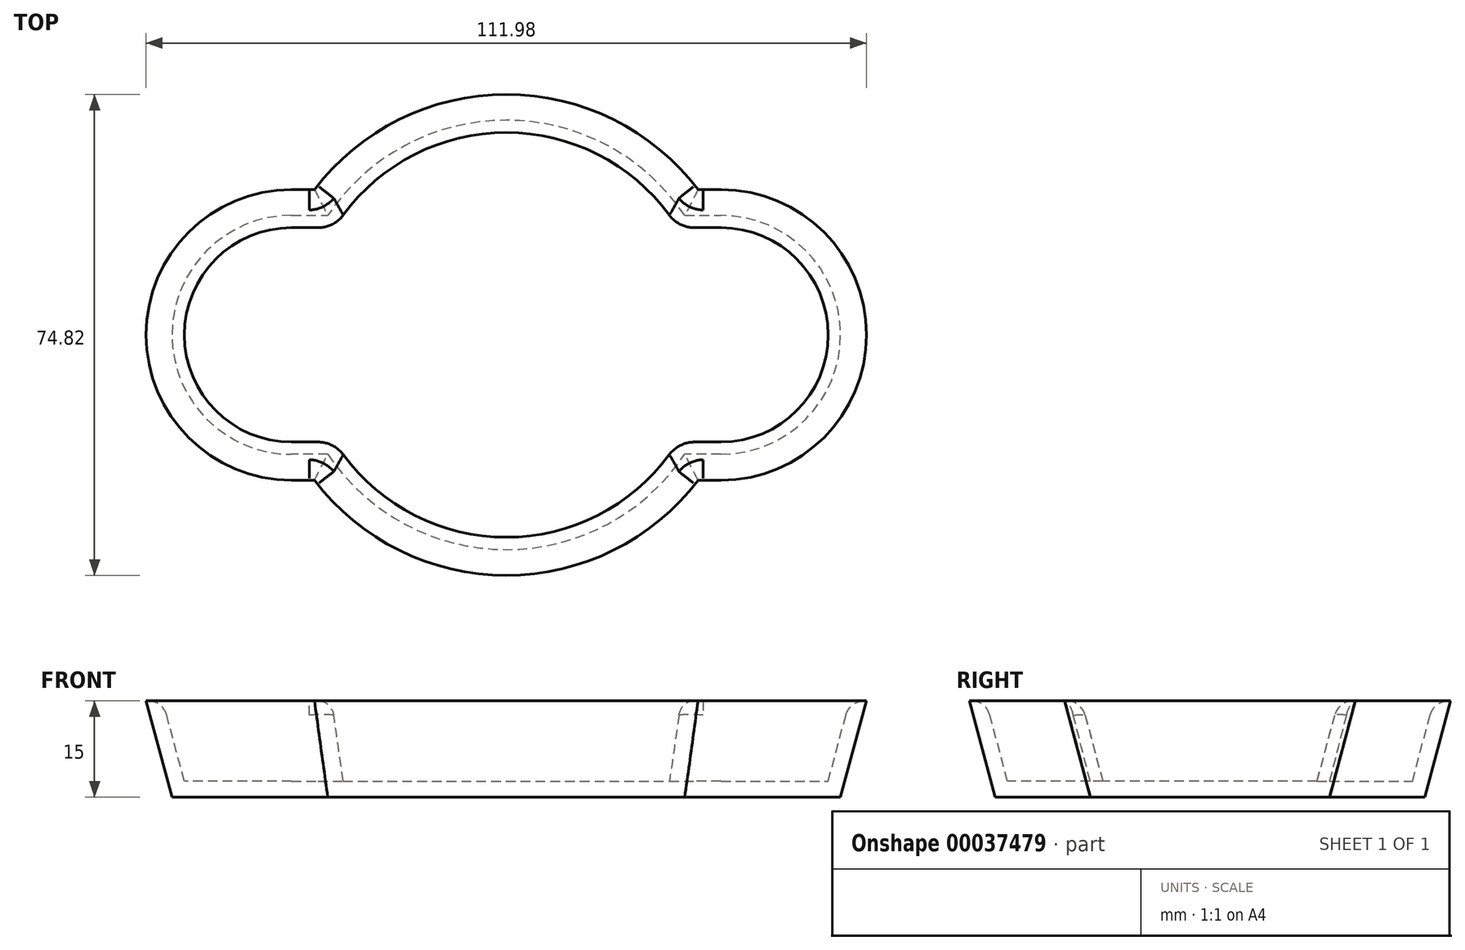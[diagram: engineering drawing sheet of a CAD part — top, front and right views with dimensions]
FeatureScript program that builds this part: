
annotation { "Feature Type Name" : "Feature", "Feature Type Description" : "" }
export const myFeature = defineFeature(function(context is Context, id is Id, definition is map)
    precondition{}
    {
        {
            var Q0;
            Q0=qCreatedBy(makeId("Top.planeOp"),FACE);
            var sketch = newSketch(context, id + "F0", { "sketchPlane" : qUnion([Q0])});
            skArc(sketch, "E0", {"start": v(-27.74, -18.58) * mm, "mid": v(0, -33.39) * mm, "end": v(27.74, -18.58) * mm});
            skArc(sketch, "E1", {"start": v(33.39, -18.58) * mm, "mid": v(51.97, 0) * mm, "end": v(33.39, 18.58) * mm});
            skLineSegment(sketch, "E2", {"start": v(0, 58.58) * mm, "end": v(0, -59.96) * mm, "construction": true});
            skArc(sketch, "E3.MirrorC", {"start": v(-33.39, -18.58) * mm, "mid": v(-51.97, 0) * mm, "end": v(-33.39, 18.58) * mm});
            skArc(sketch, "E4.trimOffspring", {"start": v(27.74, 18.58) * mm, "mid": v(0, 33.39) * mm, "end": v(-27.74, 18.58) * mm});
            skLineSegment(sketch, "E5", {"start": v(-33.39, 18.58) * mm, "end": v(-27.74, 18.58) * mm});
            skLineSegment(sketch, "E6", {"start": v(-33.39, -18.58) * mm, "end": v(-27.74, -18.58) * mm});
            skLineSegment(sketch, "E7.trimOffspring", {"start": v(27.74, 18.58) * mm, "end": v(33.39, 18.58) * mm});
            skLineSegment(sketch, "E8.trimOffspring", {"start": v(27.74, -18.58) * mm, "end": v(33.39, -18.58) * mm});
            skSolve(sketch);
        }
        {
            var Q0;
            Q0=qCreatedBy(makeId("Top.planeOp"),FACE);
            cPlane(context, id + "F1", {"entities" : qUnion([Q0]), "cplaneType" : CPlaneType.OFFSET, "offset" : 15 * mm, "width" : 152.4 * mm, "height" : 152.4 * mm});
        }
        {
            var Q0;
            Q0 = qSketchRegion(id + "F0", true);
            extrude(context, id + "F2", {"entities" : qUnion([Q0]), "depth" : 15 * mm, "hasDraft" : true, "draftAngle" : 15 * degree});
        }
        {
            var Q0;
            Q0=makeQuery(id+"F2.opExtrude","CAP_FACE",FACE,{"disambiguationData":[OSD([sQuery(id+"F0.wireOp",EDGE,"E0"),sQuery(id+"F0.wireOp",EDGE,"E1"),sQuery(id+"F0.wireOp",EDGE,"E3.MirrorC"),sQuery(id+"F0.wireOp",EDGE,"E4.trimOffspring"),sQuery(id+"F0.wireOp",EDGE,"E5"),sQuery(id+"F0.wireOp",EDGE,"E6"),sQuery(id+"F0.wireOp",EDGE,"E7.trimOffspring"),sQuery(id+"F0.wireOp",EDGE,"E8.trimOffspring")])],"isStart":false});
            shell(context, id + "F3", {"entities" : qUnion([Q0]), "thickness" : 2.5 * mm});
        }
        {
            var Q0;
            {var subQ0=sQuery(id+"F0.wireOp",EDGE,"E3.MirrorC");Q0=makeQuery(id+"F3.opShell","OFFSET_EDGE",EDGE,{"disambiguationData":[OSD([subQ0]),TDD([makeQuery(id+"F2.opExtrude","CAP_EDGE",EDGE,{"disambiguationData":[OSD([subQ0])],"isStart":false})])]});}
            var Q1;
            {var subQ0=sQuery(id+"F0.wireOp",EDGE,"E4.trimOffspring");Q1=makeQuery(id+"F3.opShell","OFFSET_EDGE",EDGE,{"disambiguationData":[OSD([subQ0]),TDD([makeQuery(id+"F2.opExtrude","CAP_EDGE",EDGE,{"disambiguationData":[OSD([subQ0])],"isStart":false})])]});}
            var Q2;
            {var subQ0=sQuery(id+"F0.wireOp",EDGE,"E5");Q2=makeQuery(id+"F3.opShell","OFFSET_EDGE",EDGE,{"disambiguationData":[OSD([subQ0]),TDD([makeQuery(id+"F2.opExtrude","CAP_EDGE",EDGE,{"disambiguationData":[OSD([subQ0])],"isStart":false})])]});}
            var Q3;
            {var subQ0=sQuery(id+"F0.wireOp",EDGE,"E7.trimOffspring");Q3=makeQuery(id+"F3.opShell","OFFSET_EDGE",EDGE,{"disambiguationData":[OSD([subQ0]),TDD([makeQuery(id+"F2.opExtrude","CAP_EDGE",EDGE,{"disambiguationData":[OSD([subQ0])],"isStart":false})])]});}
            var Q4;
            {var subQ0=sQuery(id+"F0.wireOp",EDGE,"E1");Q4=makeQuery(id+"F3.opShell","OFFSET_EDGE",EDGE,{"disambiguationData":[OSD([subQ0]),TDD([makeQuery(id+"F2.opExtrude","CAP_EDGE",EDGE,{"disambiguationData":[OSD([subQ0])],"isStart":false})])]});}
            var Q5;
            {var subQ0=sQuery(id+"F0.wireOp",EDGE,"E0");Q5=makeQuery(id+"F3.opShell","OFFSET_EDGE",EDGE,{"disambiguationData":[OSD([subQ0]),TDD([makeQuery(id+"F2.opExtrude","CAP_EDGE",EDGE,{"disambiguationData":[OSD([subQ0])],"isStart":false})])]});}
            var Q6;
            {var subQ0=sQuery(id+"F0.wireOp",EDGE,"E8.trimOffspring");Q6=makeQuery(id+"F3.opShell","OFFSET_EDGE",EDGE,{"disambiguationData":[OSD([subQ0]),TDD([makeQuery(id+"F2.opExtrude","CAP_EDGE",EDGE,{"disambiguationData":[OSD([subQ0])],"isStart":false})])]});}
            var Q7;
            {var subQ0=sQuery(id+"F0.wireOp",EDGE,"E6");Q7=makeQuery(id+"F3.opShell","OFFSET_EDGE",EDGE,{"disambiguationData":[OSD([subQ0]),TDD([makeQuery(id+"F2.opExtrude","CAP_EDGE",EDGE,{"disambiguationData":[OSD([subQ0])],"isStart":false})])]});}
            fillet(context, id + "F4", {"entities" : qUnion([Q0, Q1, Q2, Q3, Q4, Q5, Q6, Q7]), "radius" : 3 * mm, "tangentPropagation" : true, "allowEdgeOverflow" : false});
        }
        {
            var Q0;
            {var subQ0=sQuery(id+"F0.wireOp",EDGE,"E6");var subQ1=sQuery(id+"F0.wireOp",EDGE,"E0");Q0=makeQuery(id+"F4.opFillet","BLEND_EDGE",EDGE,{"blendedFrom":[makeQuery(id+"F3.opShell","OFFSET_EDGE",EDGE,{"disambiguationData":[OSD([subQ1]),TDD([makeQuery(id+"F2.opExtrude","CAP_EDGE",EDGE,{"disambiguationData":[OSD([subQ1])],"isStart":false})])]}),makeQuery(id+"F3.opShell","OFFSET_EDGE",EDGE,{"disambiguationData":[OSD([subQ0]),TDD([makeQuery(id+"F2.opExtrude","CAP_EDGE",EDGE,{"disambiguationData":[OSD([subQ0])],"isStart":false})])]})],"blendedInto":[]});}
            var Q1;
            Q1=makeQuery(id+"F3.opShell","OFFSET_EDGE",EDGE,{"disambiguationData":[OSD([sQuery(id+"F0.wireOp",EDGE,"E0"),sQuery(id+"F0.wireOp",EDGE,"E6")])]});
            var Q2;
            {var subQ0=sQuery(id+"F0.wireOp",EDGE,"E8.trimOffspring");var subQ1=sQuery(id+"F0.wireOp",EDGE,"E0");Q2=makeQuery(id+"F4.opFillet","BLEND_EDGE",EDGE,{"blendedFrom":[makeQuery(id+"F3.opShell","OFFSET_EDGE",EDGE,{"disambiguationData":[OSD([subQ1]),TDD([makeQuery(id+"F2.opExtrude","CAP_EDGE",EDGE,{"disambiguationData":[OSD([subQ1])],"isStart":false})])]}),makeQuery(id+"F3.opShell","OFFSET_EDGE",EDGE,{"disambiguationData":[OSD([subQ0]),TDD([makeQuery(id+"F2.opExtrude","CAP_EDGE",EDGE,{"disambiguationData":[OSD([subQ0])],"isStart":false})])]})],"blendedInto":[]});}
            var Q3;
            Q3=makeQuery(id+"F3.opShell","OFFSET_EDGE",EDGE,{"disambiguationData":[OSD([sQuery(id+"F0.wireOp",EDGE,"E0"),sQuery(id+"F0.wireOp",EDGE,"E8.trimOffspring")])]});
            var Q4;
            {var subQ0=sQuery(id+"F0.wireOp",EDGE,"E7.trimOffspring");var subQ1=sQuery(id+"F0.wireOp",EDGE,"E4.trimOffspring");Q4=makeQuery(id+"F4.opFillet","BLEND_EDGE",EDGE,{"blendedFrom":[makeQuery(id+"F3.opShell","OFFSET_EDGE",EDGE,{"disambiguationData":[OSD([subQ1]),TDD([makeQuery(id+"F2.opExtrude","CAP_EDGE",EDGE,{"disambiguationData":[OSD([subQ1])],"isStart":false})])]}),makeQuery(id+"F3.opShell","OFFSET_EDGE",EDGE,{"disambiguationData":[OSD([subQ0]),TDD([makeQuery(id+"F2.opExtrude","CAP_EDGE",EDGE,{"disambiguationData":[OSD([subQ0])],"isStart":false})])]})],"blendedInto":[]});}
            var Q5;
            Q5=makeQuery(id+"F3.opShell","OFFSET_EDGE",EDGE,{"disambiguationData":[OSD([sQuery(id+"F0.wireOp",EDGE,"E4.trimOffspring"),sQuery(id+"F0.wireOp",EDGE,"E7.trimOffspring")])]});
            var Q6;
            Q6=makeQuery(id+"F3.opShell","OFFSET_EDGE",EDGE,{"disambiguationData":[OSD([sQuery(id+"F0.wireOp",EDGE,"E4.trimOffspring"),sQuery(id+"F0.wireOp",EDGE,"E5")])]});
            var Q7;
            {var subQ0=sQuery(id+"F0.wireOp",EDGE,"E5");var subQ1=sQuery(id+"F0.wireOp",EDGE,"E4.trimOffspring");Q7=makeQuery(id+"F4.opFillet","BLEND_EDGE",EDGE,{"blendedFrom":[makeQuery(id+"F3.opShell","OFFSET_EDGE",EDGE,{"disambiguationData":[OSD([subQ1]),TDD([makeQuery(id+"F2.opExtrude","CAP_EDGE",EDGE,{"disambiguationData":[OSD([subQ1])],"isStart":false})])]}),makeQuery(id+"F3.opShell","OFFSET_EDGE",EDGE,{"disambiguationData":[OSD([subQ0]),TDD([makeQuery(id+"F2.opExtrude","CAP_EDGE",EDGE,{"disambiguationData":[OSD([subQ0])],"isStart":false})])]})],"blendedInto":[]});}
            var Q8;
            {var subQ0=sQuery(id+"F0.wireOp",EDGE,"E5");Q8=makeQuery(id+"F4.opFillet","BLEND_EDGE",EDGE,{"blendedFrom":[makeQuery(id+"F3.opShell","OFFSET_EDGE",EDGE,{"disambiguationData":[OSD([subQ0]),TDD([makeQuery(id+"F2.opExtrude","CAP_EDGE",EDGE,{"disambiguationData":[OSD([subQ0])],"isStart":false})])]}),makeQuery(id+"F3.opShell","OFFSET_FACE",FACE,{"disambiguationData":[OSD([subQ0])]})],"blendedInto":[makeQuery(id+"F3.opShell","OFFSET_FACE",FACE,{"disambiguationData":[OSD([subQ0])]})]});}
            var Q9;
            {var subQ0=sQuery(id+"F0.wireOp",EDGE,"E4.trimOffspring");Q9=makeQuery(id+"F4.opFillet","BLEND_EDGE",EDGE,{"blendedFrom":[makeQuery(id+"F3.opShell","OFFSET_EDGE",EDGE,{"disambiguationData":[OSD([subQ0]),TDD([makeQuery(id+"F2.opExtrude","CAP_EDGE",EDGE,{"disambiguationData":[OSD([subQ0])],"isStart":false})])]}),makeQuery(id+"F3.opShell","OFFSET_FACE",FACE,{"disambiguationData":[OSD([subQ0])]})],"blendedInto":[makeQuery(id+"F3.opShell","OFFSET_FACE",FACE,{"disambiguationData":[OSD([subQ0])]})]});}
            fillet(context, id + "F5", {"entities" : qUnion([Q0, Q1, Q2, Q3, Q4, Q5, Q6, Q7, Q8, Q9]), "radius" : 5 * mm, "tangentPropagation" : true, "allowEdgeOverflow" : false});
        }
    });
